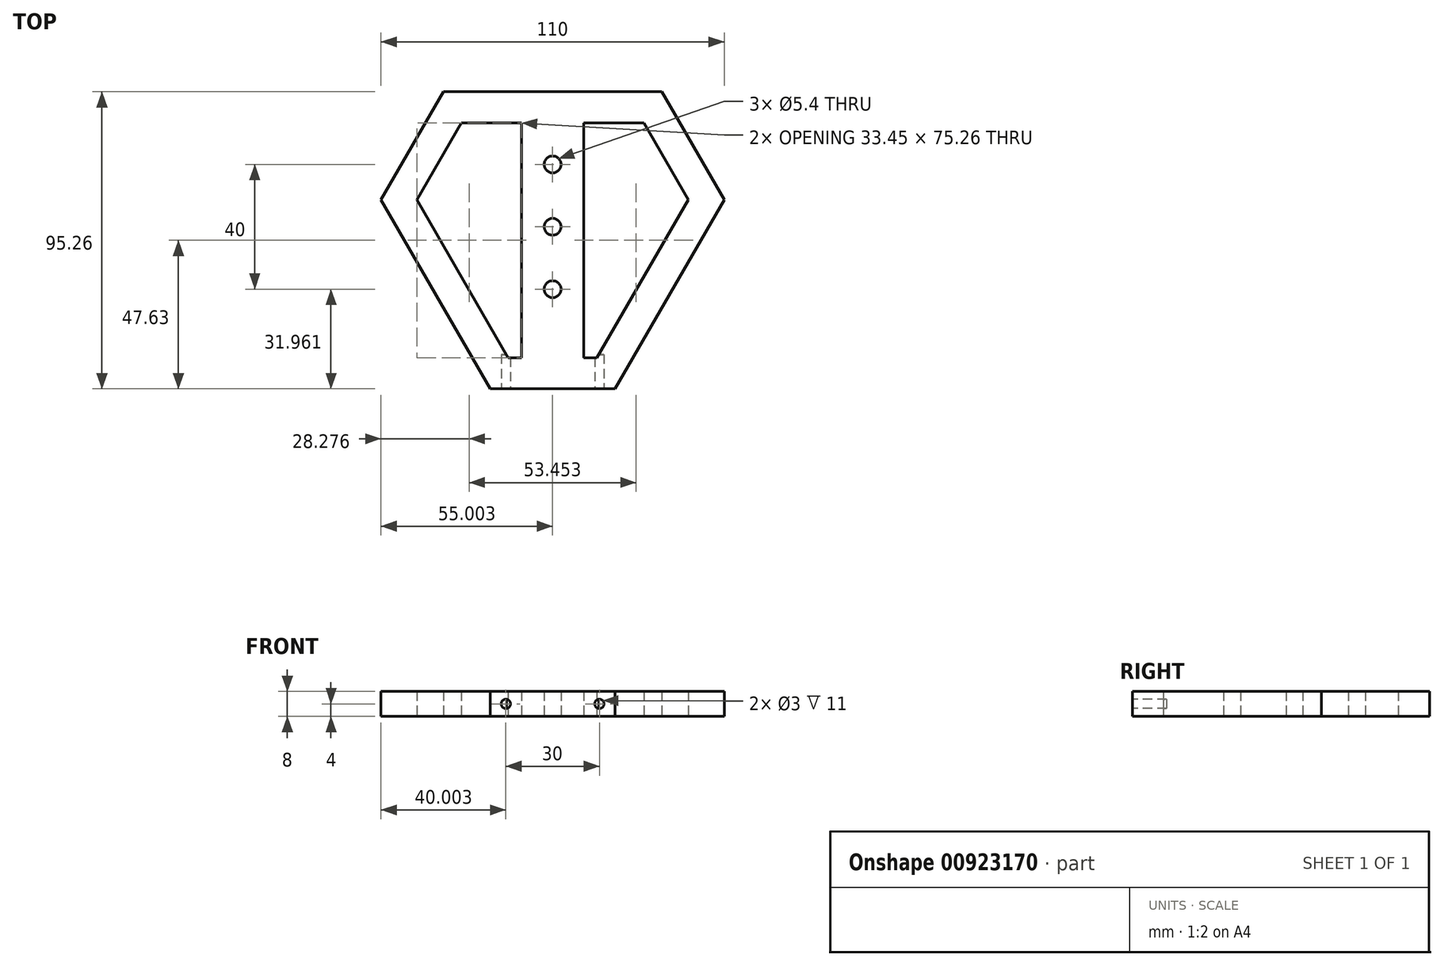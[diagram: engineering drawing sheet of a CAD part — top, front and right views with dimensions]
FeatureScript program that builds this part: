
annotation { "Feature Type Name" : "Feature", "Feature Type Description" : "" }
export const myFeature = defineFeature(function(context is Context, id is Id, definition is map)
    precondition{}
    {
        {
            var Q0;
            Q0=qCreatedBy(makeId("Top.planeOp"),FACE);
            var sketch = newSketch(context, id + "F0", { "sketchPlane" : qUnion([Q0])});
            skLineSegment(sketch, "E0", {"start": v(-39.02, 105.04) * mm, "end": v(30.98, 105.04) * mm});
            skLineSegment(sketch, "E1", {"start": v(30.98, 105.04) * mm, "end": v(50.98, 70.4) * mm});
            skLineSegment(sketch, "E2", {"start": v(50.98, 70.4) * mm, "end": v(15.98, 9.78) * mm});
            skLineSegment(sketch, "E3", {"start": v(15.98, 9.78) * mm, "end": v(-24.02, 9.78) * mm});
            skLineSegment(sketch, "E4", {"start": v(-24.02, 9.78) * mm, "end": v(-59.02, 70.4) * mm});
            skLineSegment(sketch, "E5", {"start": v(-59.02, 70.4) * mm, "end": v(-39.02, 105.04) * mm});
            skLineSegment(sketch, "E6.0", {"start": v(39.44, 70.4) * mm, "end": v(10.2, 19.78) * mm});
            skLineSegment(sketch, "E6.1", {"start": v(-18.24, 19.78) * mm, "end": v(-47.47, 70.4) * mm});
            skLineSegment(sketch, "E6.2", {"start": v(-47.47, 70.4) * mm, "end": v(-33.24, 95.04) * mm});
            skLineSegment(sketch, "E6.3", {"start": v(10.2, 19.78) * mm, "end": v(5.98, 19.78) * mm});
            skLineSegment(sketch, "E6.4", {"start": v(-33.24, 95.04) * mm, "end": v(-14.02, 95.04) * mm});
            skLineSegment(sketch, "E6.5", {"start": v(25.2, 95.04) * mm, "end": v(39.44, 70.4) * mm});
            skLineSegment(sketch, "E7", {"start": v(-4.02, 105.04) * mm, "end": v(-4.02, 9.78) * mm, "construction": true});
            skLineSegment(sketch, "E8", {"start": v(-41.52, 40.09) * mm, "end": v(40.98, 87.72) * mm, "construction": true});
            skLineSegment(sketch, "E9", {"start": v(33.48, 40.09) * mm, "end": v(-49.02, 87.72) * mm, "construction": true});
            skPoint(sketch, "E10", {"position": v(-4.02, 61.74) * mm});
            skLineSegment(sketch, "E11.left", {"start": v(-14.02, 95.04) * mm, "end": v(-14.02, 19.78) * mm});
            skLineSegment(sketch, "E11.right", {"start": v(5.98, 95.04) * mm, "end": v(5.98, 19.78) * mm});
            skCircle(sketch, "E12", {"center": v(-4.02, 61.74) * mm, "radius": 2.7 * mm});
            skCircle(sketch, "E13", {"center": v(-4.02, 81.74) * mm, "radius": 2.7 * mm});
            skCircle(sketch, "E14", {"center": v(-4.02, 41.74) * mm, "radius": 2.7 * mm});
            skLineSegment(sketch, "E15.trimOffspring", {"start": v(5.98, 95.04) * mm, "end": v(25.2, 95.04) * mm});
            skLineSegment(sketch, "E16.trimOffspring", {"start": v(-14.02, 19.78) * mm, "end": v(-18.24, 19.78) * mm});
            skSolve(sketch);
        }
        {
            var Q0;
            Q0 = qSketchRegion(id + "F0", true);
            extrude(context, id + "F1", {"entities" : qUnion([Q0]), "depth" : 8 * mm, "offsetDistance" : 25 * mm});
        }
        {
            var Q0;
            Q0=makeQuery(id+"F1.opExtrude","SWEPT_FACE",FACE,{"disambiguationData":[OSD([sQuery(id+"F0.wireOp",EDGE,"E3")])]});
            var sketch = newSketch(context, id + "F2", { "sketchPlane" : qUnion([Q0])});
            skLineSegment(sketch, "E17", {"start": v(-24.02, 4) * mm, "end": v(15.98, 4) * mm, "construction": true});
            skLineSegment(sketch, "E18", {"start": v(-4.02, 8) * mm, "end": v(-4.02, 0) * mm, "construction": true});
            skCircle(sketch, "E19", {"center": v(10.98, 4) * mm, "radius": 1.5 * mm});
            skCircle(sketch, "E20", {"center": v(-19.02, 4) * mm, "radius": 1.5 * mm});
            skSolve(sketch);
        }
        {
            var Q0;
            Q0 = qSketchRegion(id + "F2", true);
            extrude(context, id + "F3", {"entities" : qUnion([Q0]), "operationType" : NewBodyOperationType.REMOVE, "oppositeDirection" : true, "depth" : 11 * mm, "offsetDistance" : 25 * mm});
        }
    });
